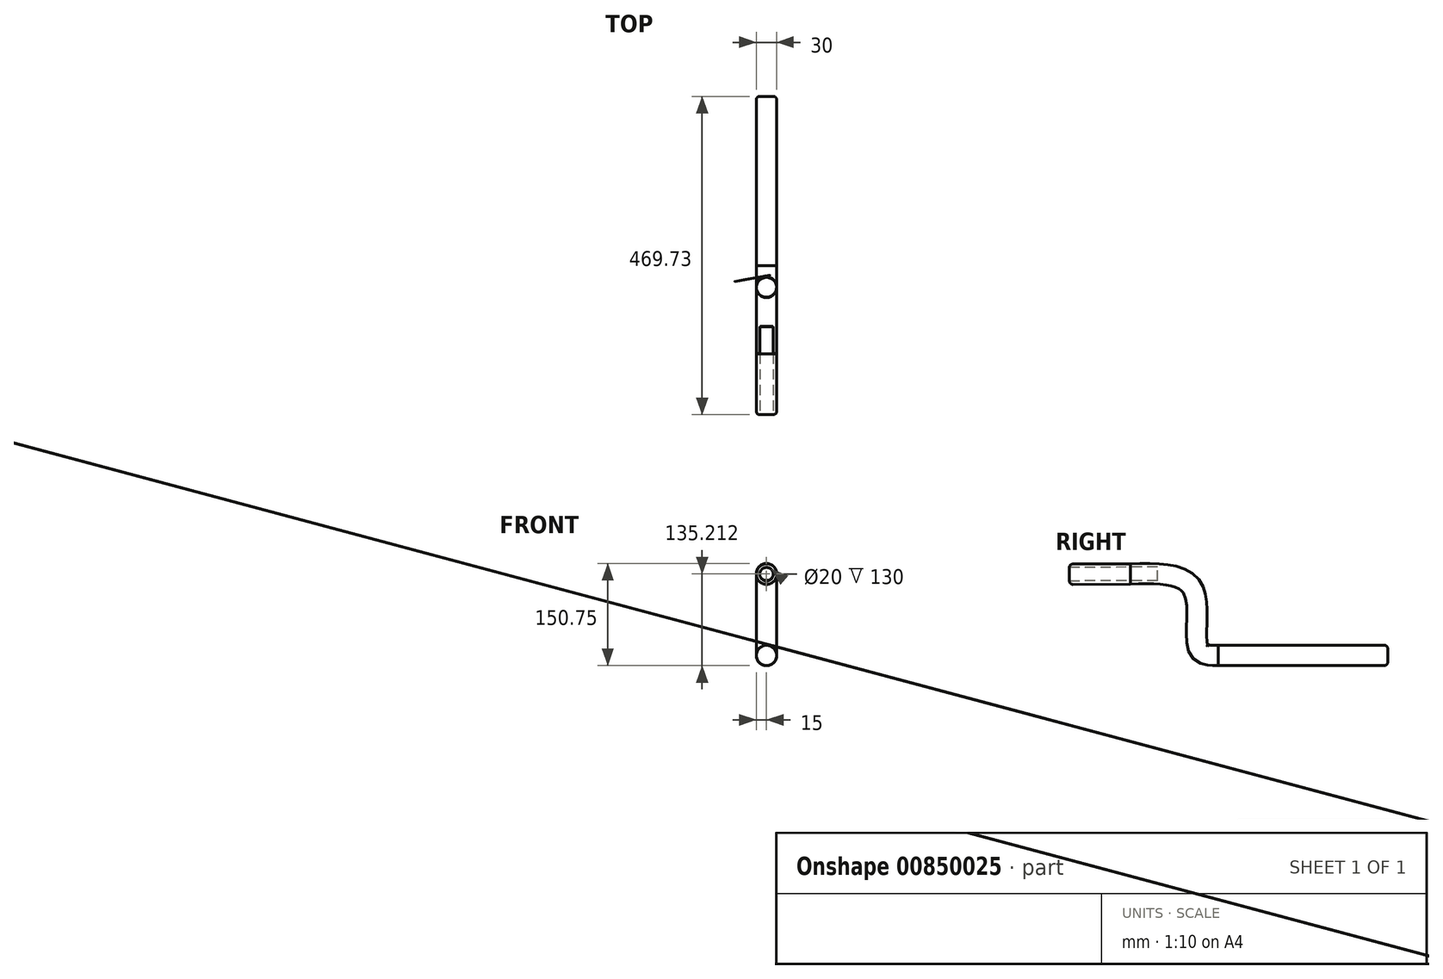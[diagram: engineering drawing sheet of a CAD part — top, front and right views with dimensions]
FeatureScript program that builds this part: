
annotation { "Feature Type Name" : "Feature", "Feature Type Description" : "" }
export const myFeature = defineFeature(function(context is Context, id is Id, definition is map)
    precondition{}
    {
        {
            var Q0;
            Q0=qCreatedBy(makeId("Front.planeOp"),FACE);
            var sketch = newSketch(context, id + "F0", { "sketchPlane" : qUnion([Q0])});
            skCircle(sketch, "E0", {"center": v(0, 0) * mm, "radius": 15 * mm});
            skSolve(sketch);
        }
        {
            var Q0;
            Q0=qCreatedBy(makeId("Right.planeOp"),FACE);
            var sketch = newSketch(context, id + "F1", { "sketchPlane" : qUnion([Q0])});
            skFitSpline(sketch, "E1", {"points": [v(0, 0) * mm, v(-28.96, 9.65) * mm, v(-37.31, 97.84) * mm, v(-129.67, 120.28) * mm], "startDerivative": vector(-161.38, -3.18) * mm, "endDerivative": vector(-301.66, -7.65) * mm});
            skSolve(sketch);
        }
        {
            var Q0;
            Q0=makeQuery(id+"F0.imprint","IMPRINT",FACE,{"disambiguationData":[TD([[makeQuery(id+"F0.imprint","IMPRINT",EDGE,{"derivedFrom":sQuery(id+"F0.wireOp",EDGE,"E0")}),1.0]])]});
            var Q1;
            Q1=sQuery(id+"F1.wireOp",EDGE,"E1");
            sweep(context, id + "F2", {"profiles" : qUnion([Q0]), "path" : qUnion([Q1])});
        }
        {
            var Q0;
            Q0=makeQuery(id+"F2.opSweep","CAP_FACE",FACE,{"disambiguationData":[OSD([sQuery(id+"F0.wireOp",EDGE,"E0"),sQuery(id+"F1.wireOp",VERTEX,"E1.start")])],"isStart":true});
            extrude(context, id + "F3", {"entities" : qUnion([Q0]), "operationType" : NewBodyOperationType.ADD, "depth" : 250 * mm, "offsetDistance" : 25 * mm});
        }
        {
            var Q0;
            Q0=makeQuery(id+"F2.opSweep","CAP_FACE",FACE,{"disambiguationData":[OSD([sQuery(id+"F0.wireOp",EDGE,"E0"),sQuery(id+"F1.wireOp",VERTEX,"E1.end")])],"isStart":false});
            extrude(context, id + "F4", {"entities" : qUnion([Q0]), "operationType" : NewBodyOperationType.ADD, "depth" : 90 * mm, "offsetDistance" : 25 * mm});
        }
        {
            var Q0;
            Q0=makeQuery(id+"F4.opExtrude","CAP_FACE",FACE,{"disambiguationData":[OSD([sQuery(id+"F0.wireOp",EDGE,"E0"),sQuery(id+"F1.wireOp",VERTEX,"E1.end")])],"isStart":false});
            var sketch = newSketch(context, id + "F5", { "sketchPlane" : qUnion([Q0])});
            skCircle(sketch, "E2", {"center": v(0, 121) * mm, "radius": 10 * mm});
            skSolve(sketch);
        }
        {
            var Q0;
            Q0=makeQuery(id+"F5.imprint","IMPRINT",FACE,{"disambiguationData":[TD([[makeQuery(id+"F5.imprint","IMPRINT",EDGE,{"derivedFrom":sQuery(id+"F5.wireOp",EDGE,"E2")}),1.0]])]});
            extrude(context, id + "F6", {"entities" : qUnion([Q0]), "operationType" : NewBodyOperationType.REMOVE, "oppositeDirection" : true, "depth" : 130 * mm, "offsetDistance" : 25 * mm});
        }
        {
            var Q0;
            Q0=makeQuery(id+"F2.opSweep","SWEPT_FACE",FACE,{"disambiguationData":[OSD([sQuery(id+"F0.wireOp",EDGE,"E0"),sQuery(id+"F1.wireOp",EDGE,"E1")])]});
            var Q1;
            Q1=makeQuery(id+"F4.opExtrude","SWEPT_FACE",FACE,{"disambiguationData":[OSD([sQuery(id+"F0.wireOp",EDGE,"E0"),sQuery(id+"F1.wireOp",VERTEX,"E1.end")])]});
            var Q2;
            Q2=makeQuery(id+"F3.opExtrude","SWEPT_FACE",FACE,{"disambiguationData":[OSD([sQuery(id+"F0.wireOp",EDGE,"E0"),sQuery(id+"F1.wireOp",VERTEX,"E1.start")])]});
            fillet(context, id + "F7", {"entities" : qUnion([Q0, Q1, Q2]), "radius" : 5 * mm, "tangentPropagation" : true, "allowEdgeOverflow" : false});
        }
    });
